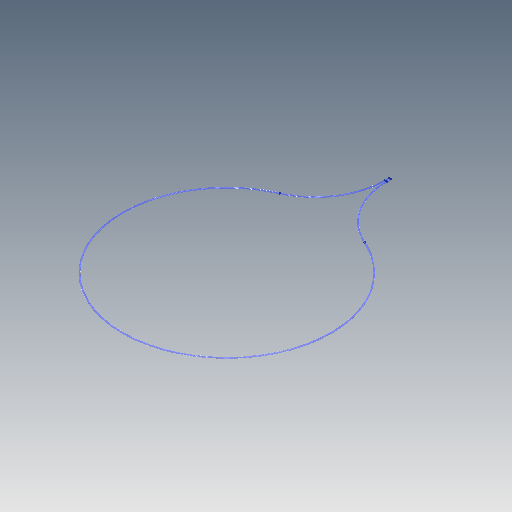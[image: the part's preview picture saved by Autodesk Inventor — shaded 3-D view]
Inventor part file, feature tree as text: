
AUTODESK INVENTOR PART (.ipt)
format: ipt  version: 2020 (Build 240168000, 168)  size: 192,000 bytes
history: native  units: mm
features: extrude x2, sketch x2, projected_geometry x2, fillet x1, shell x1
ambient origin geometry x8: Origin, YZ Plane, XZ Plane, XY Plane, X Axis, Y Axis, Z Axis, Center Point
bodies: Solid1 (feature_tree)
feature tree (8):
  extrude  "Extrusion1"  Depth=1.0mm
  fillet  "Fillet1"  Radius=0.15mm
  extrude  "Extrusion2"  Depth=0.5mm
  shell  "Shell1"  Thickness=0.0mm
  sketch  "Sketch1"  dims[d16=0.15mm d17=1.0mm d18=0.15mm]
  sketch  "Sketch2"  dims[d19=150.0mm d20=0.15mm d21=1.0mm d22=0.15mm d23=100.0mm d24=0.05mm d25=1.0mm d26=100.0mm d27=10.0mm d28=0.15mm d29=1.0mm d30=0.15mm d31=100.0mm d32=0.05mm d33=1.0mm d34=100.0mm d35=10.0mm d36=1.0mm d37=0.0mm d38=0.5mm d39=3.0mm d40=0.0mm d41=0.02mm]
  projected_geometry  "Projected Loop1"
  projected_geometry  "Projected Loop2"
